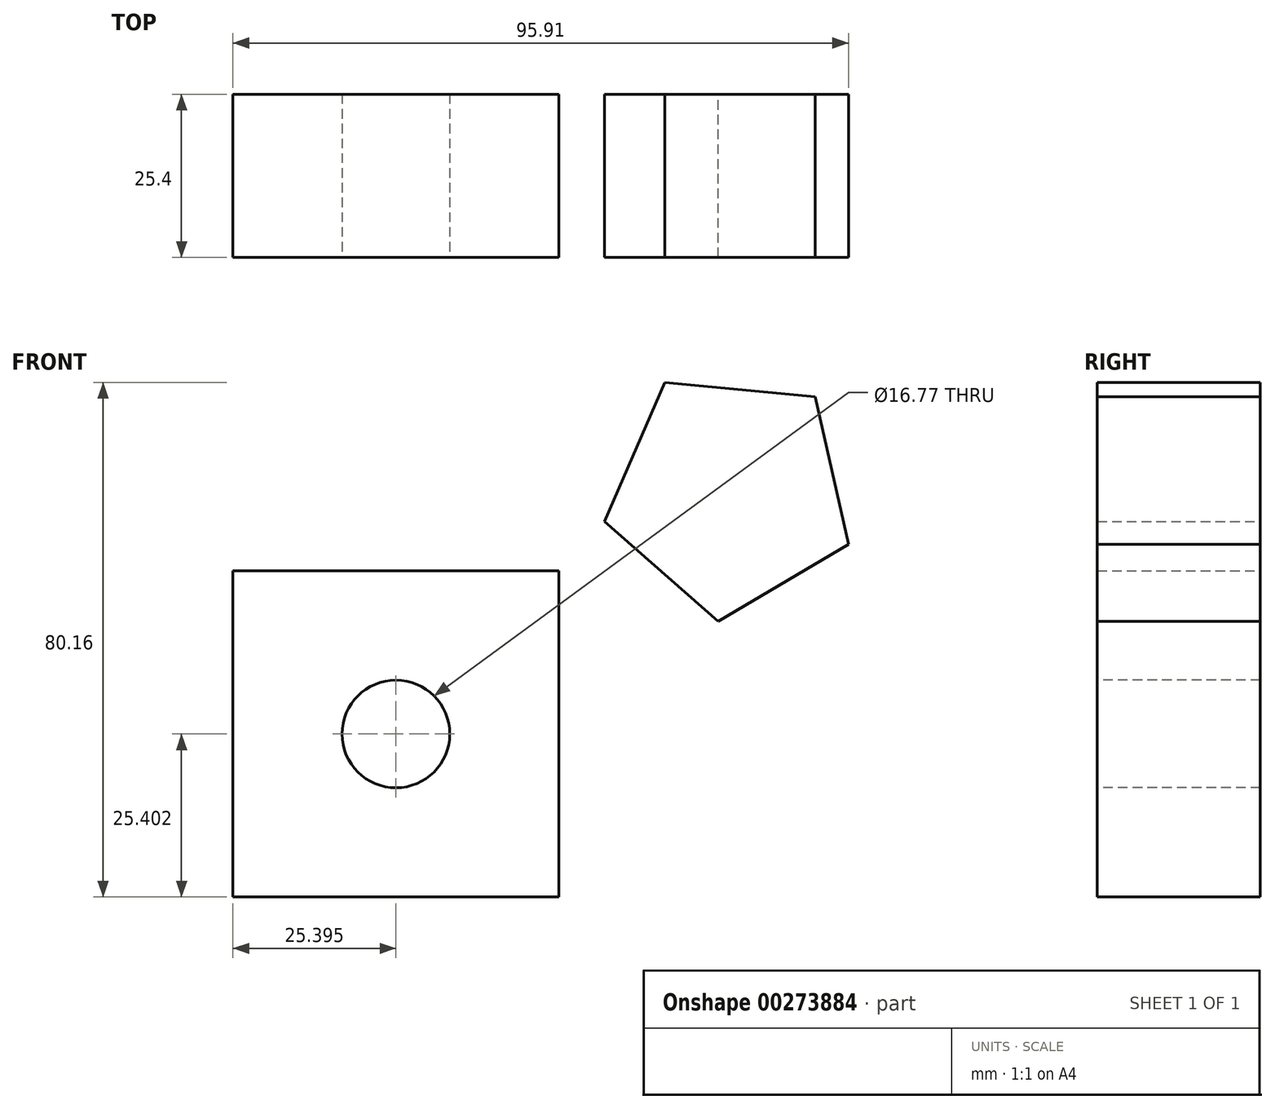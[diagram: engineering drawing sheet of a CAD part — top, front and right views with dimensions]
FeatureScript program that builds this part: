
annotation { "Feature Type Name" : "Feature", "Feature Type Description" : "" }
export const myFeature = defineFeature(function(context is Context, id is Id, definition is map)
    precondition{}
    {
        {
            var Q0;
            Q0=qCreatedBy(makeId("Front.planeOp"),FACE);
            var sketch = newSketch(context, id + "F0", { "sketchPlane" : qUnion([Q0])});
            skLineSegment(sketch, "E0.bottom", {"start": v(-36.77, 36.88) * mm, "end": v(14.03, 36.88) * mm});
            skLineSegment(sketch, "E0.top", {"start": v(-36.77, -13.92) * mm, "end": v(14.03, -13.92) * mm});
            skLineSegment(sketch, "E0.left", {"start": v(-36.77, 36.88) * mm, "end": v(-36.77, -13.92) * mm});
            skLineSegment(sketch, "E0.right", {"start": v(14.03, 36.88) * mm, "end": v(14.03, -13.92) * mm});
            skSolve(sketch);
        }
        {
            var Q0;
            Q0 = qSketchRegion(id + "F0", true);
            extrude(context, id + "F1", {"entities" : qUnion([Q0]), "depth" : 25.4 * mm});
        }
        {
            var Q0;
            Q0=makeQuery(id+"F1.opExtrude","CAP_FACE",FACE,{"disambiguationData":[OSD([sQuery(id+"F0.wireOp",EDGE,"E0.bottom"),sQuery(id+"F0.wireOp",EDGE,"E0.top"),sQuery(id+"F0.wireOp",EDGE,"E0.left"),sQuery(id+"F0.wireOp",EDGE,"E0.right")])],"isStart":false});
            var sketch = newSketch(context, id + "F2", { "sketchPlane" : qUnion([Q0])});
            skLineSegment(sketch, "E1", {"start": v(-11.37, -13.92) * mm, "end": v(14.03, 11.48) * mm});
            skLineSegment(sketch, "E2", {"start": v(-36.77, 11.48) * mm, "end": v(-11.37, 36.88) * mm});
            skLineSegment(sketch, "E3", {"start": v(14.03, 11.48) * mm, "end": v(-11.37, 36.88) * mm});
            skLineSegment(sketch, "E4", {"start": v(-11.37, -13.92) * mm, "end": v(-36.77, 11.48) * mm});
            skCircle(sketch, "E5", {"center": v(-11.37, 11.48) * mm, "radius": 8.39 * mm});
            skSolve(sketch);
        }
        {
            var Q0;
            Q0=makeQuery(id+"F2.imprint","IMPRINT",FACE,{"disambiguationData":[TD([[makeQuery(id+"F2.imprint","IMPRINT",EDGE,{"derivedFrom":sQuery(id+"F2.wireOp",EDGE,"E5")}),1.0]])]});
            extrude(context, id + "F3", {"entities" : qUnion([Q0]), "operationType" : NewBodyOperationType.REMOVE, "endBound" : BoundingType.THROUGH_ALL, "oppositeDirection" : true, "depth" : 25.4 * mm});
        }
        {
            var Q0;
            Q0=qCreatedBy(makeId("Front.planeOp"),FACE);
            var sketch = newSketch(context, id + "F4", { "sketchPlane" : qUnion([Q0])});
            skCircle(sketch, "E6.cCircle", {"center": v(40.73, 48.99) * mm, "radius": 16.23 * mm, "construction": true});
            skLineSegment(sketch, "E6.0", {"start": v(59.14, 41.04) * mm, "end": v(38.86, 29.02) * mm});
            skLineSegment(sketch, "E6.1", {"start": v(38.86, 29.02) * mm, "end": v(21.16, 44.6) * mm});
            skLineSegment(sketch, "E6.2", {"start": v(21.16, 44.6) * mm, "end": v(30.5, 66.24) * mm});
            skLineSegment(sketch, "E6.3", {"start": v(30.5, 66.24) * mm, "end": v(53.98, 64.05) * mm});
            skLineSegment(sketch, "E6.4", {"start": v(53.98, 64.05) * mm, "end": v(59.14, 41.04) * mm});
            skPoint(sketch, "E6.0.midPoint", {"position": v(49, 35.03) * mm});
            skSolve(sketch);
        }
        {
            var Q0;
            Q0 = qSketchRegion(id + "F4", true);
            extrude(context, id + "F5", {"entities" : qUnion([Q0]), "depth" : 25.4 * mm});
        }
    });
